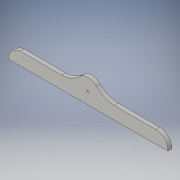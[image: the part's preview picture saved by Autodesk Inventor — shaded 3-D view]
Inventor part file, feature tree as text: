
AUTODESK INVENTOR PART (.ipt)
format: ipt  version: 2016 (Build 200138000, 138)  size: 368,640 bytes
history: native  units: in
note: dims shown in document units (in); Inventor stores cm internally (conversion verified against a paired STEP export)
features: extrude x1, hole x1, sketch x1
ambient origin geometry x8: Origin, YZ Plane, XZ Plane, XY Plane, X Axis, Y Axis, Z Axis, Center Point
bodies: Body1 (feature_tree)
feature tree (3):
  extrude  "Extrusion2"  Depth=0.25in TaperAngle=0.0deg
  hole  "Hole3"  [1 undecoded]
  sketch  "Sketch1"  dims[d2=0.76in d13=0.25in d14=0.0in d58=0.76in d62=0.1in d63=0.75in d64=0.375in d65=0.25in d66=0.5635in d67=0.1in d68=0.8108in d74=10.0in d75=0.8in d76=1.5in d78=1.6727in d79=0.7328in d87=0.75in d89=2.6in d90=2.6in d91=0.8669in d92=0.7584in d93=0.8603in d36=1.0in d37=1.0in]
note: 1 required parameter value undecoded (feature->parameter linkage not recoverable at this tier; creation-order binding heuristic only, values carry confidence <= 0.55)
